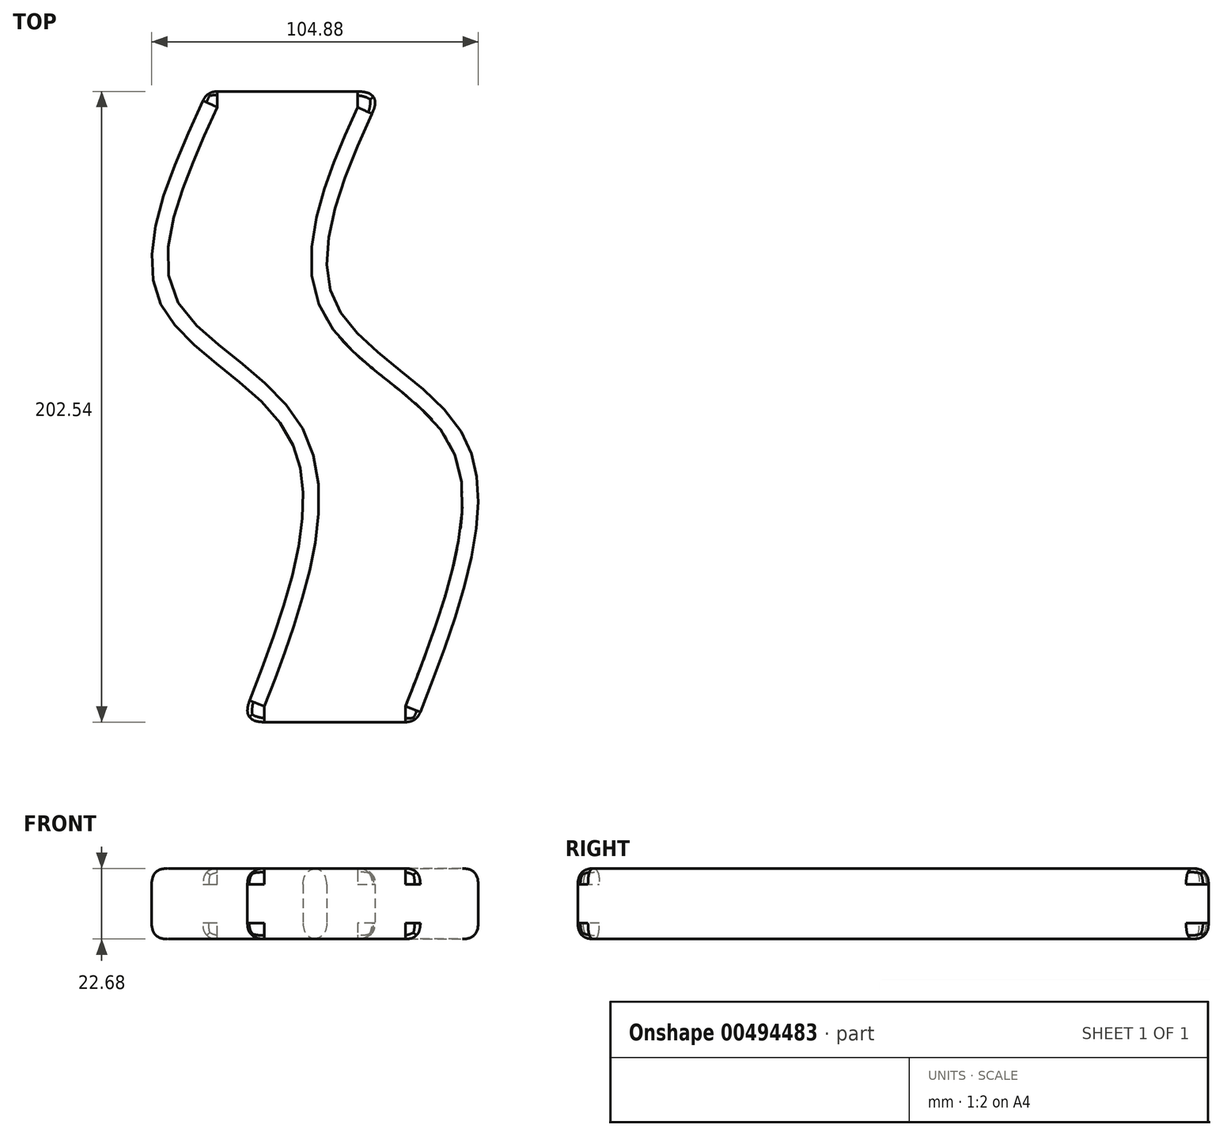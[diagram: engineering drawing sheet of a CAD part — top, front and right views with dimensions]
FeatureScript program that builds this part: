
annotation { "Feature Type Name" : "Feature", "Feature Type Description" : "" }
export const myFeature = defineFeature(function(context is Context, id is Id, definition is map)
    precondition{}
    {
        {
            var Q0;
            Q0=qCreatedBy(makeId("Front.planeOp"),FACE);
            var sketch = newSketch(context, id + "F0", { "sketchPlane" : qUnion([Q0])});
            skLineSegment(sketch, "E0.bottom", {"start": v(-9.32, -15.13) * mm, "end": v(46.9, -15.13) * mm});
            skLineSegment(sketch, "E0.top", {"start": v(-9.32, 7.55) * mm, "end": v(46.9, 7.55) * mm});
            skLineSegment(sketch, "E0.left", {"start": v(-9.32, -15.13) * mm, "end": v(-9.32, 7.55) * mm});
            skLineSegment(sketch, "E0.right", {"start": v(46.9, -15.13) * mm, "end": v(46.9, 7.55) * mm});
            skSolve(sketch);
        }
        {
            var Q0;
            Q0=qCreatedBy(makeId("Top.planeOp"),FACE);
            var sketch = newSketch(context, id + "F1", { "sketchPlane" : qUnion([Q0])});
            skFitSpline(sketch, "E1", {"points": [v(-15.76, -90.84) * mm, v(0, 0) * mm, v(-41.76, 43.75) * mm, v(-26.68, 111.7) * mm], "startDerivative": vector(107.87, 276.7) * mm, "endDerivative": vector(108.02, 233.26) * mm});
            skSolve(sketch);
        }
        {
            var Q0;
            Q0=makeQuery(id+"F0.imprint","IMPRINT",FACE,{"disambiguationData":[TD([[makeQuery(id+"F0.imprint","IMPRINT",EDGE,{"derivedFrom":sQuery(id+"F0.wireOp",EDGE,"E0.bottom")}),1.0]])]});
            var Q1;
            Q1=sQuery(id+"F1.wireOp",EDGE,"E1");
            sweep(context, id + "F2", {"profiles" : qUnion([Q0]), "path" : qUnion([Q1]), "keepProfileOrientation" : true});
        }
        {
            var Q0;
            Q0=makeQuery(id+"F2.opSweep","SWEPT_FACE",FACE,{"disambiguationData":[OSD([sQuery(id+"F0.wireOp",EDGE,"E0.top"),sQuery(id+"F1.wireOp",EDGE,"E1")])]});
            var Q1;
            Q1=makeQuery(id+"F2.opSweep","SWEPT_FACE",FACE,{"disambiguationData":[OSD([sQuery(id+"F0.wireOp",EDGE,"E0.right"),sQuery(id+"F1.wireOp",EDGE,"E1")])]});
            var Q2;
            Q2=makeQuery(id+"F2.opSweep","CAP_FACE",FACE,{"disambiguationData":[OSD([sQuery(id+"F0.wireOp",EDGE,"E0.bottom"),sQuery(id+"F0.wireOp",EDGE,"E0.top"),sQuery(id+"F0.wireOp",EDGE,"E0.left"),sQuery(id+"F0.wireOp",EDGE,"E0.right"),sQuery(id+"F1.wireOp",VERTEX,"E1.start")])],"isStart":true});
            var Q3;
            Q3=makeQuery(id+"F2.opSweep","SWEPT_FACE",FACE,{"disambiguationData":[OSD([sQuery(id+"F0.wireOp",EDGE,"E0.bottom"),sQuery(id+"F1.wireOp",EDGE,"E1")])]});
            var Q4;
            Q4=makeQuery(id+"F2.opSweep","SWEPT_FACE",FACE,{"disambiguationData":[OSD([sQuery(id+"F0.wireOp",EDGE,"E0.left"),sQuery(id+"F1.wireOp",EDGE,"E1")])]});
            fillet(context, id + "F3", {"entities" : qUnion([Q0, Q1, Q2, Q3, Q4]), "radius" : 5.08 * mm, "tangentPropagation" : true, "rho" : 0.5, "crossSection" : FilletCrossSection.CONIC, "allowEdgeOverflow" : false});
        }
    });
